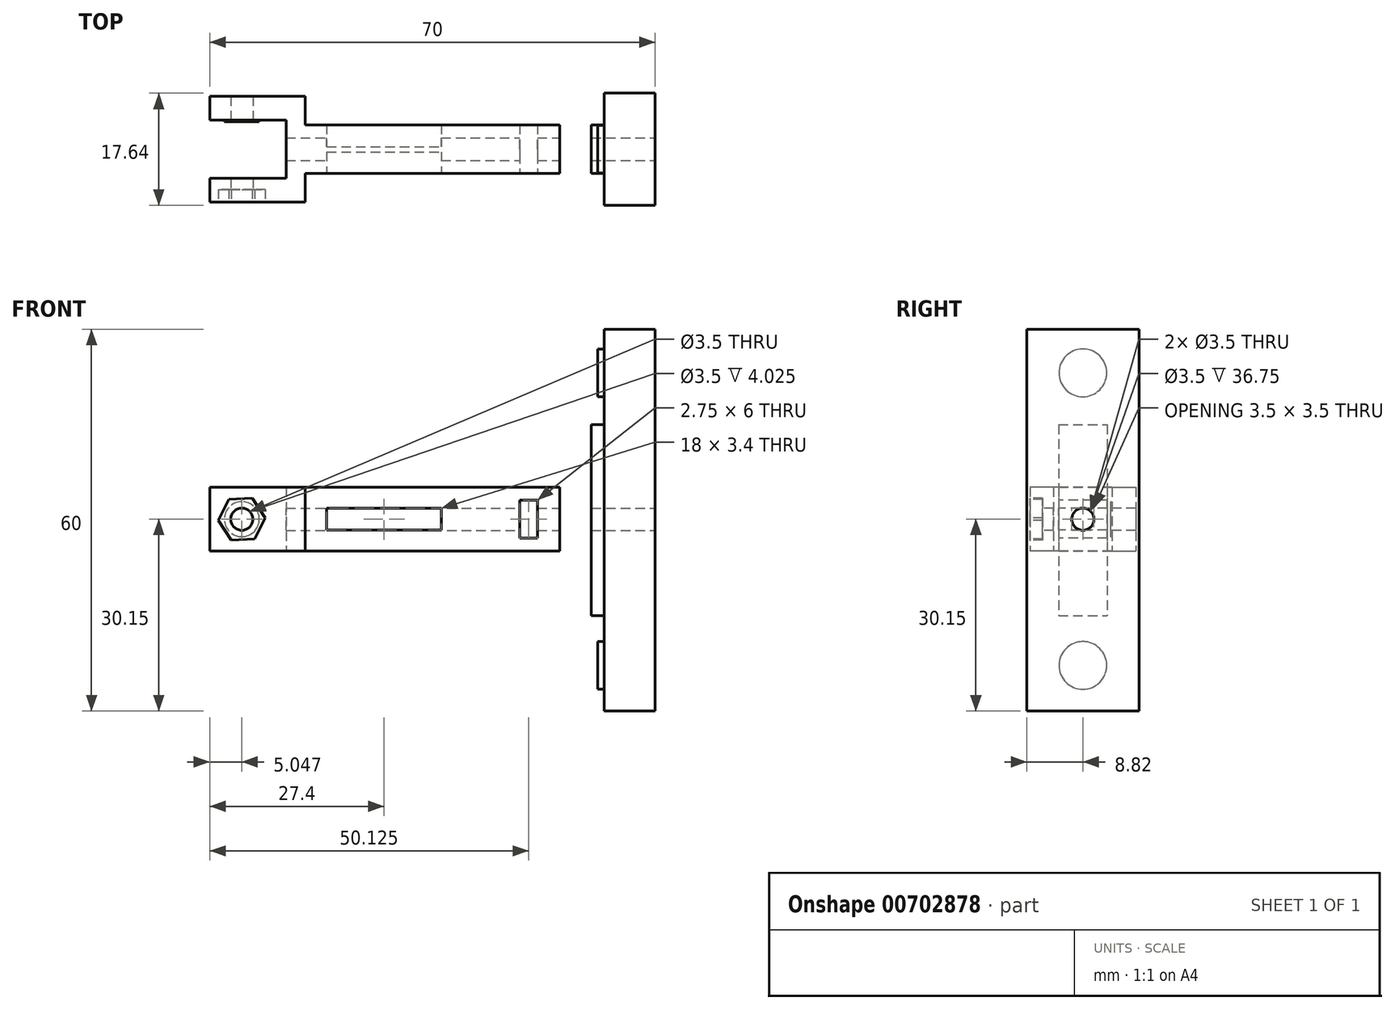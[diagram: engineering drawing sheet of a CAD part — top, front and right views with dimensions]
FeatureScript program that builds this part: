
annotation { "Feature Type Name" : "Feature", "Feature Type Description" : "" }
export const myFeature = defineFeature(function(context is Context, id is Id, definition is map)
    precondition{}
    {
        {
            var Q0;
            Q0=qCreatedBy(makeId("Top.planeOp"),FACE);
            var sketch = newSketch(context, id + "F0", { "sketchPlane" : qUnion([Q0])});
            skLineSegment(sketch, "E0.bottom", {"start": v(0, 0) * mm, "end": v(40, 0) * mm});
            skLineSegment(sketch, "E0.top", {"start": v(0, -3.83) * mm, "end": v(40, -3.83) * mm});
            skLineSegment(sketch, "E0.left", {"start": v(0, 0) * mm, "end": v(0, -3.83) * mm});
            skLineSegment(sketch, "E0.right", {"start": v(40, 0) * mm, "end": v(40, -3.83) * mm});
            skLineSegment(sketch, "E1.bottom", {"start": v(-3, 0) * mm, "end": v(0, 0) * mm});
            skLineSegment(sketch, "E1.top", {"start": v(-15, -8.32) * mm, "end": v(0, -8.32) * mm});
            skLineSegment(sketch, "E1.left", {"start": v(-15, -4.6) * mm, "end": v(-15, -8.32) * mm});
            skLineSegment(sketch, "E1.right", {"start": v(0, 0) * mm, "end": v(0, -8.32) * mm});
            skLineSegment(sketch, "E2.top", {"start": v(-15, -4.6) * mm, "end": v(-3, -4.6) * mm});
            skLineSegment(sketch, "E2.right", {"start": v(-3, 0) * mm, "end": v(-3, -4.6) * mm});
            skLineSegment(sketch, "E3.MirrorCS", {"start": v(0, 0) * mm, "end": v(0, 3.83) * mm});
            skLineSegment(sketch, "E4.MirrorCS", {"start": v(0, 0) * mm, "end": v(0, 8.32) * mm});
            skLineSegment(sketch, "E5.MirrorCS", {"start": v(-15, 4.6) * mm, "end": v(-15, 8.32) * mm});
            skLineSegment(sketch, "E6.MirrorCS", {"start": v(-3, 0) * mm, "end": v(-3, 4.6) * mm});
            skLineSegment(sketch, "E7.MirrorCS", {"start": v(-15, 8.32) * mm, "end": v(0, 8.32) * mm});
            skLineSegment(sketch, "E8.MirrorCS", {"start": v(-15, 4.6) * mm, "end": v(-3, 4.6) * mm});
            skLineSegment(sketch, "E9.MirrorCS", {"start": v(40, 0) * mm, "end": v(40, 3.83) * mm});
            skLineSegment(sketch, "E10.MirrorCS", {"start": v(0, 3.83) * mm, "end": v(40, 3.83) * mm});
            skSolve(sketch);
        }
        {
            var Q0;
            {var subQ2=sQuery(id+"F0.wireOp",EDGE,"E1.top");Q0=makeQuery(id+"F0.imprint","IMPRINT",FACE,{"disambiguationData":[TD([[makeQuery(id+"F0.imprint","IMPRINT",EDGE,{"derivedFrom":subQ2}),1.0]])]});}
            var Q1;
            Q1=makeQuery(id+"F0.imprint","IMPRINT",FACE,{"disambiguationData":[TD([[makeQuery(id+"F0.imprint","IMPRINT",EDGE,{"derivedFrom":sQuery(id+"F0.wireOp",EDGE,"E5.MirrorCS")}),-1.0]])]});
            var Q2;
            {var subQ0=sQuery(id+"F0.wireOp",EDGE,"E0.bottom");Q2=makeQuery(id+"F0.imprint","IMPRINT",FACE,{"disambiguationData":[TD([[makeQuery(id+"F0.imprint","IMPRINT",EDGE,{"derivedFrom":subQ0}),1.0]])]});}
            var Q3;
            {var subQ0=sQuery(id+"F0.wireOp",EDGE,"E0.bottom");Q3=makeQuery(id+"F0.imprint","IMPRINT",FACE,{"disambiguationData":[TD([[makeQuery(id+"F0.imprint","IMPRINT",EDGE,{"derivedFrom":subQ0}),-1.0]])]});}
            extrude(context, id + "F1", {"entities" : qUnion([Q0, Q1, Q2, Q3]), "depth" : 10 * mm});
        }
        {
            var Q0;
            Q0=makeQuery(id+"F1.opExtrude","SWEPT_FACE",FACE,{"disambiguationData":[OSD([sQuery(id+"F0.wireOp",EDGE,"E1.top")])]});
            var sketch = newSketch(context, id + "F2", { "sketchPlane" : qUnion([Q0])});
            skCircle(sketch, "E11", {"center": v(-9.95, 5) * mm, "radius": 1.75 * mm});
            skSolve(sketch);
        }
        {
            var Q0;
            Q0=makeQuery(id+"F2.imprint","IMPRINT",FACE,{"disambiguationData":[TD([[makeQuery(id+"F2.imprint","IMPRINT",EDGE,{"derivedFrom":sQuery(id+"F2.wireOp",EDGE,"E11")}),1.0]])]});
            extrude(context, id + "F3", {"entities" : qUnion([Q0]), "operationType" : NewBodyOperationType.REMOVE, "endBound" : BoundingType.THROUGH_ALL, "oppositeDirection" : true, "depth" : 25 * mm});
        }
        {
            var Q0;
            Q0=makeQuery(id+"F1.opExtrude","SWEPT_FACE",FACE,{"disambiguationData":[OSD([sQuery(id+"F0.wireOp",EDGE,"E0.top")])]});
            var sketch = newSketch(context, id + "F4", { "sketchPlane" : qUnion([Q0])});
            skLineSegment(sketch, "E12.bottom", {"start": v(3.4, 3.3) * mm, "end": v(21.4, 3.3) * mm});
            skLineSegment(sketch, "E12.top", {"start": v(3.4, 6.7) * mm, "end": v(21.4, 6.7) * mm});
            skLineSegment(sketch, "E12.left", {"start": v(3.4, 3.3) * mm, "end": v(3.4, 6.7) * mm});
            skLineSegment(sketch, "E12.right", {"start": v(21.4, 3.3) * mm, "end": v(21.4, 6.7) * mm});
            skLineSegment(sketch, "E13.bottom", {"start": v(33.75, 8) * mm, "end": v(36.5, 8) * mm});
            skLineSegment(sketch, "E13.top", {"start": v(33.75, 2) * mm, "end": v(36.5, 2) * mm});
            skLineSegment(sketch, "E13.left", {"start": v(33.75, 8) * mm, "end": v(33.75, 2) * mm});
            skLineSegment(sketch, "E13.right", {"start": v(36.5, 8) * mm, "end": v(36.5, 2) * mm});
            skSolve(sketch);
        }
        {
            var Q0;
            Q0=makeQuery(id+"F4.imprint","IMPRINT",FACE,{"disambiguationData":[TD([[makeQuery(id+"F4.imprint","IMPRINT",EDGE,{"derivedFrom":sQuery(id+"F4.wireOp",EDGE,"E12.bottom")}),1.0]])]});
            var Q1;
            Q1=makeQuery(id+"F4.imprint","IMPRINT",FACE,{"disambiguationData":[TD([[makeQuery(id+"F4.imprint","IMPRINT",EDGE,{"derivedFrom":sQuery(id+"F4.wireOp",EDGE,"E13.bottom")}),-1.0]])]});
            extrude(context, id + "F5", {"entities" : qUnion([Q0, Q1]), "operationType" : NewBodyOperationType.REMOVE, "endBound" : BoundingType.THROUGH_ALL, "oppositeDirection" : true, "depth" : 25 * mm});
        }
        {
            var Q0;
            Q0=makeQuery(id+"F1.opExtrude","SWEPT_FACE",FACE,{"disambiguationData":[OSD([sQuery(id+"F0.wireOp",EDGE,"E0.right"),sQuery(id+"F0.wireOp",EDGE,"E9.MirrorCS")])]});
            var sketch = newSketch(context, id + "F6", { "sketchPlane" : qUnion([Q0])});
            skCircle(sketch, "E14", {"center": v(0, 5) * mm, "radius": 1.75 * mm});
            skSolve(sketch);
        }
        {
            var Q0;
            Q0=makeQuery(id+"F6.imprint","IMPRINT",FACE,{"disambiguationData":[TD([[makeQuery(id+"F6.imprint","IMPRINT",EDGE,{"derivedFrom":sQuery(id+"F6.wireOp",EDGE,"E14")}),1.0]])]});
            extrude(context, id + "F7", {"entities" : qUnion([Q0]), "operationType" : NewBodyOperationType.REMOVE, "oppositeDirection" : true, "depth" : 15 * mm});
        }
        {
            var Q0;
            Q0=makeQuery(id+"F1.opExtrude","SWEPT_FACE",FACE,{"disambiguationData":[OSD([sQuery(id+"F0.wireOp",EDGE,"E0.right"),sQuery(id+"F0.wireOp",EDGE,"E9.MirrorCS")])]});
            cPlane(context, id + "F8", {"entities" : qUnion([Q0]), "cplaneType" : CPlaneType.OFFSET, "offset" : 5 * mm, "width" : 150 * mm, "height" : 150 * mm});
        }
        {
            var Q0;
            Q0=qCreatedBy(id+"F8.planeOp",FACE);
            var sketch = newSketch(context, id + "F9", { "sketchPlane" : qUnion([Q0])});
            skLineSegment(sketch, "E15.0", {"start": v(3.83, 10) * mm, "end": v(3.83, 0) * mm});
            skLineSegment(sketch, "E16.0", {"start": v(-3.82, 10) * mm, "end": v(-3.82, 0) * mm});
            skLineSegment(sketch, "E17.bottom", {"start": v(-3.82, 19.85) * mm, "end": v(3.83, 19.85) * mm});
            skLineSegment(sketch, "E17.top", {"start": v(-3.82, -10.15) * mm, "end": v(3.83, -10.15) * mm});
            skLineSegment(sketch, "E17.left", {"start": v(-3.82, 19.85) * mm, "end": v(-3.82, -10.15) * mm});
            skLineSegment(sketch, "E17.right", {"start": v(3.83, 19.85) * mm, "end": v(3.83, -10.15) * mm});
            skPoint(sketch, "E18.oppositeSnap0", {"position": v(3.83, 4.85) * mm});
            skLineSegment(sketch, "E18.bottom", {"start": v(3.83, 4.85) * mm, "end": v(3.83, 4.85) * mm});
            skLineSegment(sketch, "E18.top", {"start": v(3.83, 4.85) * mm, "end": v(3.83, 4.85) * mm});
            skLineSegment(sketch, "E18.left", {"start": v(3.83, 4.85) * mm, "end": v(3.83, 4.85) * mm});
            skLineSegment(sketch, "E18.right", {"start": v(3.83, 4.85) * mm, "end": v(3.83, 4.85) * mm});
            skSolve(sketch);
        }
        {
            var Q0;
            {var subQ0=sQuery(id+"F9.wireOp",EDGE,"E17.bottom");Q0=makeQuery(id+"F9.imprint","IMPRINT",FACE,{"disambiguationData":[TD([[makeQuery(id+"F9.imprint","IMPRINT",EDGE,{"derivedFrom":subQ0}),-1.0]])]});}
            extrude(context, id + "F10", {"entities" : qUnion([Q0]), "depth" : 2 * mm});
        }
        {
            var Q0;
            Q0=makeQuery(id+"F10.opExtrude","CAP_FACE",FACE,{"disambiguationData":[OSD([sQuery(id+"F9.wireOp",EDGE,"E17.bottom"),sQuery(id+"F9.wireOp",EDGE,"E17.top"),sQuery(id+"F9.wireOp",EDGE,"E17.left"),sQuery(id+"F9.wireOp",EDGE,"E17.right")])],"isStart":false});
            var sketch = newSketch(context, id + "F11", { "sketchPlane" : qUnion([Q0])});
            skLineSegment(sketch, "E19.bottom", {"start": v(8.82, 34.85) * mm, "end": v(-8.83, 34.85) * mm});
            skLineSegment(sketch, "E19.top", {"start": v(8.83, -25.15) * mm, "end": v(-8.82, -25.15) * mm});
            skLineSegment(sketch, "E19.left", {"start": v(8.82, 34.85) * mm, "end": v(8.83, -25.15) * mm});
            skLineSegment(sketch, "E19.right", {"start": v(-8.83, 34.85) * mm, "end": v(-8.82, -25.15) * mm});
            skSolve(sketch);
        }
        {
            var Q0;
            Q0=qSketchRegion(id+"F11",true);
            extrude(context, id + "F12", {"entities" : qUnion([Q0]), "operationType" : NewBodyOperationType.ADD, "depth" : 8 * mm});
        }
        {
            var Q0;
            Q0=makeQuery(id+"F12.opExtrude","CAP_FACE",FACE,{"disambiguationData":[OSD([sQuery(id+"F11.wireOp",EDGE,"E19.bottom"),sQuery(id+"F11.wireOp",EDGE,"E19.top"),sQuery(id+"F11.wireOp",EDGE,"E19.left"),sQuery(id+"F11.wireOp",EDGE,"E19.right")])],"isStart":false});
            var sketch = newSketch(context, id + "F13", { "sketchPlane" : qUnion([Q0])});
            skCircle(sketch, "E20.0", {"center": v(0, 5) * mm, "radius": 1.75 * mm});
            skSolve(sketch);
        }
        {
            var Q0;
            Q0=makeQuery(id+"F13.imprint","IMPRINT",FACE,{"disambiguationData":[TD([[makeQuery(id+"F13.imprint","IMPRINT",EDGE,{"derivedFrom":sQuery(id+"F13.wireOp",EDGE,"E20.0")}),1.0]])]});
            extrude(context, id + "F14", {"entities" : qUnion([Q0]), "operationType" : NewBodyOperationType.REMOVE, "endBound" : BoundingType.THROUGH_ALL, "oppositeDirection" : true, "depth" : 25 * mm});
        }
        {
            var Q0;
            Q0=makeQuery(id+"F1.opExtrude","SWEPT_FACE",FACE,{"disambiguationData":[OSD([sQuery(id+"F0.wireOp",EDGE,"E8.MirrorCS")])]});
            var sketch = newSketch(context, id + "F15", { "sketchPlane" : qUnion([Q0])});
            skCircle(sketch, "E21", {"center": v(-9.95, 5) * mm, "radius": 1.75 * mm});
            skCircle(sketch, "E22", {"center": v(-9.95, 5) * mm, "radius": 2.75 * mm});
            skSolve(sketch);
        }
        {
            var Q0;
            Q0=makeQuery(id+"F15.imprint","IMPRINT",FACE,{"disambiguationData":[TD([[makeQuery(id+"F15.imprint","IMPRINT",EDGE,{"derivedFrom":sQuery(id+"F15.wireOp",EDGE,"E21")}),1.0]])]});
            extrude(context, id + "F16", {"entities" : qUnion([Q0]), "operationType" : NewBodyOperationType.ADD, "depth" : 0.3 * mm});
        }
        {
            var Q0;
            Q0=makeQuery(id+"F1.opExtrude","SWEPT_FACE",FACE,{"disambiguationData":[OSD([sQuery(id+"F0.wireOp",EDGE,"E1.top")])]});
            var sketch = newSketch(context, id + "F17", { "sketchPlane" : qUnion([Q0])});
            skCircle(sketch, "E23.cCircle", {"center": v(-9.95, 5) * mm, "radius": 3.2 * mm, "construction": true});
            skLineSegment(sketch, "E23.0", {"start": v(-6.26, 5.2) * mm, "end": v(-7.93, 1.9) * mm});
            skLineSegment(sketch, "E23.1", {"start": v(-7.93, 1.9) * mm, "end": v(-11.62, 1.7) * mm});
            skLineSegment(sketch, "E23.2", {"start": v(-11.62, 1.7) * mm, "end": v(-13.64, 4.8) * mm});
            skLineSegment(sketch, "E23.3", {"start": v(-13.64, 4.8) * mm, "end": v(-11.98, 8.1) * mm});
            skLineSegment(sketch, "E23.4", {"start": v(-11.98, 8.1) * mm, "end": v(-8.29, 8.3) * mm});
            skLineSegment(sketch, "E23.5", {"start": v(-8.29, 8.3) * mm, "end": v(-6.26, 5.2) * mm});
            skPoint(sketch, "E23.0.midPoint", {"position": v(-7.1, 3.56) * mm});
            skSolve(sketch);
        }
        {
            var Q0;
            Q0=makeQuery(id+"F17.imprint","IMPRINT",FACE,{"disambiguationData":[TD([[makeQuery(id+"F17.imprint","IMPRINT",EDGE,{"derivedFrom":sQuery(id+"F17.wireOp",EDGE,"E23.0")}),-1.0]])]});
            extrude(context, id + "F18", {"entities" : qUnion([Q0]), "operationType" : NewBodyOperationType.REMOVE, "oppositeDirection" : true, "depth" : 2 * mm});
        }
        {
            var Q0;
            Q0=makeQuery(id+"F12.opExtrude","CAP_FACE",FACE,{"disambiguationData":[OSD([sQuery(id+"F11.wireOp",EDGE,"E19.bottom"),sQuery(id+"F11.wireOp",EDGE,"E19.top"),sQuery(id+"F11.wireOp",EDGE,"E19.left"),sQuery(id+"F11.wireOp",EDGE,"E19.right")])],"isStart":true});
            var sketch = newSketch(context, id + "F19", { "sketchPlane" : qUnion([Q0])});
            skCircle(sketch, "E24.0", {"center": v(0, 5) * mm, "radius": 1.75 * mm});
            skCircle(sketch, "E25", {"center": v(0, -18) * mm, "radius": 3.75 * mm});
            skCircle(sketch, "E26", {"center": v(0, 28) * mm, "radius": 3.75 * mm});
            skSolve(sketch);
        }
        {
            var Q0;
            Q0=makeQuery(id+"F19.imprint","IMPRINT",FACE,{"disambiguationData":[TD([[makeQuery(id+"F19.imprint","IMPRINT",EDGE,{"derivedFrom":sQuery(id+"F19.wireOp",EDGE,"E26")}),1.0]])]});
            var Q1;
            Q1=makeQuery(id+"F19.imprint","IMPRINT",FACE,{"disambiguationData":[TD([[makeQuery(id+"F19.imprint","IMPRINT",EDGE,{"derivedFrom":sQuery(id+"F19.wireOp",EDGE,"E25")}),1.0]])]});
            extrude(context, id + "F20", {"entities" : qUnion([Q0, Q1]), "operationType" : NewBodyOperationType.ADD, "depth" : 1 * mm, "offsetDistance" : 25 * mm});
        }
    });
